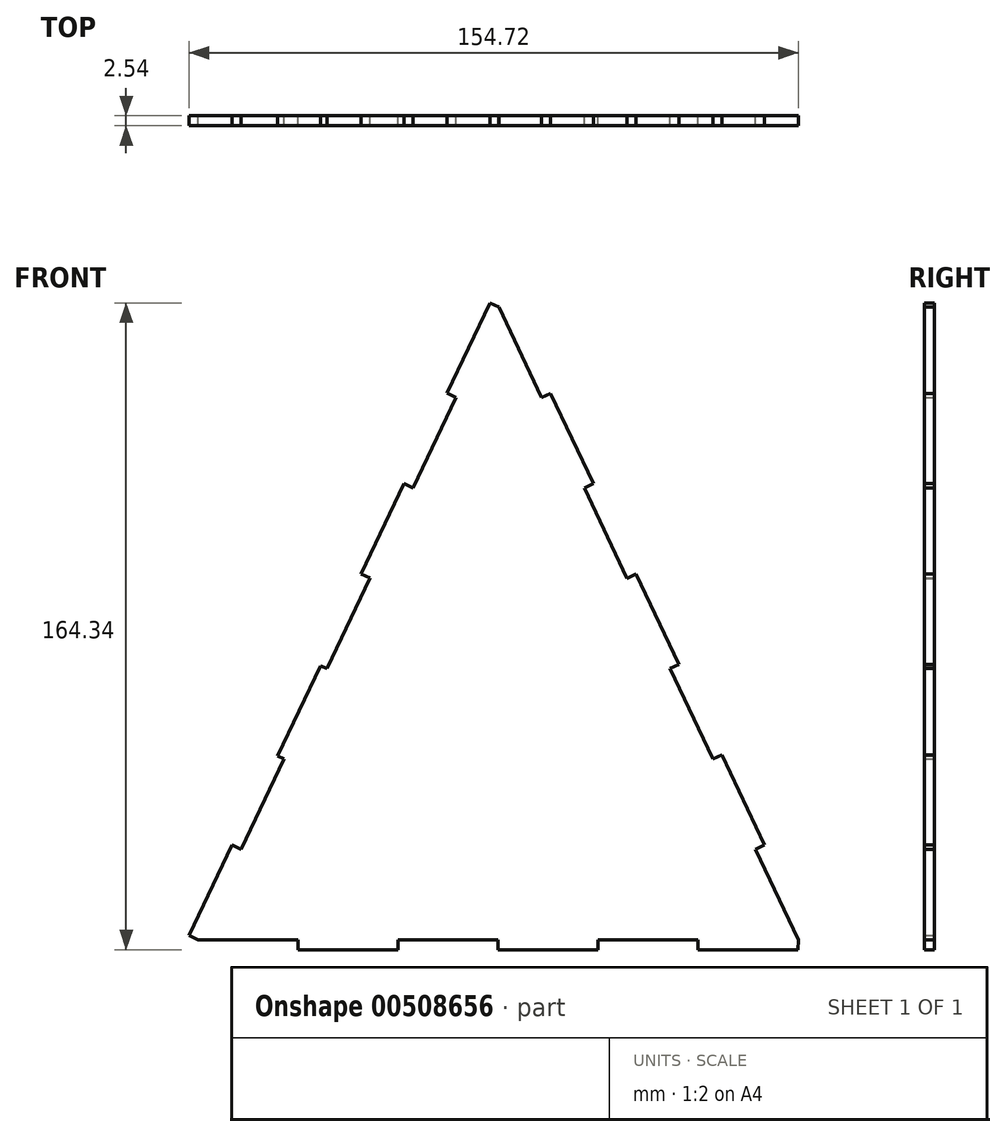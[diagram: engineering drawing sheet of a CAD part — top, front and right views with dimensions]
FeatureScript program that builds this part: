
annotation { "Feature Type Name" : "Feature", "Feature Type Description" : "" }
export const myFeature = defineFeature(function(context is Context, id is Id, definition is map)
    precondition{}
    {
        {
            var Q0;
            Q0=qCreatedBy(makeId("Front.planeOp"),FACE);
            var sketch = newSketch(context, id + "F0", { "sketchPlane" : qUnion([Q0])});
            skLineSegment(sketch, "E0", {"start": v(-10.9, 63.99) * mm, "end": v(-54.56, -27.9) * mm});
            skLineSegment(sketch, "E1", {"start": v(-76.36, -73.78) * mm, "end": v(76.06, -73.78) * mm});
            skLineSegment(sketch, "E2", {"start": v(76.06, -73.78) * mm, "end": v(0, 86.93) * mm});
            skLineSegment(sketch, "E3", {"start": v(0, 86.93) * mm, "end": v(-2.3, 88.02) * mm});
            skLineSegment(sketch, "E4", {"start": v(-2.3, 88.02) * mm, "end": v(-13.2, 65.08) * mm});
            skLineSegment(sketch, "E5", {"start": v(-13.2, 65.08) * mm, "end": v(-10.9, 63.99) * mm});
            skLineSegment(sketch, "E6", {"start": v(-24.1, 42.14) * mm, "end": v(-35, 19.2) * mm});
            skLineSegment(sketch, "E7", {"start": v(-35, 19.2) * mm, "end": v(-32.7, 18.1) * mm});
            skLineSegment(sketch, "E8", {"start": v(-43.6, -4.84) * mm, "end": v(-45.27, -4.19) * mm});
            skLineSegment(sketch, "E9", {"start": v(-45.27, -4.19) * mm, "end": v(-56.17, -27.13) * mm});
            skLineSegment(sketch, "E10", {"start": v(-56.17, -27.13) * mm, "end": v(-54.56, -27.9) * mm});
            skLineSegment(sketch, "E11", {"start": v(-54.56, -27.9) * mm, "end": v(-65.46, -50.84) * mm});
            skLineSegment(sketch, "E12", {"start": v(-65.46, -50.84) * mm, "end": v(-67.76, -49.75) * mm});
            skLineSegment(sketch, "E13", {"start": v(-67.76, -49.75) * mm, "end": v(-78.66, -72.7) * mm});
            skLineSegment(sketch, "E14", {"start": v(-78.66, -72.7) * mm, "end": v(-76.36, -73.78) * mm});
            skLineSegment(sketch, "E15", {"start": v(-76.36, -73.78) * mm, "end": v(-50.96, -73.78) * mm});
            skLineSegment(sketch, "E16", {"start": v(-50.96, -73.78) * mm, "end": v(-50.96, -76.32) * mm});
            skLineSegment(sketch, "E17", {"start": v(-50.96, -76.32) * mm, "end": v(-25.56, -76.32) * mm});
            skLineSegment(sketch, "E18", {"start": v(-25.56, -76.32) * mm, "end": v(-25.56, -73.78) * mm});
            skLineSegment(sketch, "E19", {"start": v(-25.56, -73.78) * mm, "end": v(-0.15, -73.78) * mm});
            skLineSegment(sketch, "E20", {"start": v(-0.15, -73.78) * mm, "end": v(-0.15, -76.32) * mm});
            skLineSegment(sketch, "E21", {"start": v(-0.15, -76.32) * mm, "end": v(25.25, -76.32) * mm});
            skLineSegment(sketch, "E22", {"start": v(25.25, -76.32) * mm, "end": v(25.25, -73.78) * mm});
            skLineSegment(sketch, "E23", {"start": v(25.25, -73.78) * mm, "end": v(50.65, -73.78) * mm});
            skLineSegment(sketch, "E24", {"start": v(50.65, -73.78) * mm, "end": v(50.65, -76.32) * mm});
            skPoint(sketch, "E25", {"position": v(78.35, 9.9) * mm});
            skLineSegment(sketch, "E26", {"start": v(50.65, -76.32) * mm, "end": v(76.05, -76.32) * mm});
            skLineSegment(sketch, "E27", {"start": v(76.05, -76.32) * mm, "end": v(76.06, -73.78) * mm});
            skLineSegment(sketch, "E28", {"start": v(76.06, -73.78) * mm, "end": v(65.2, -50.82) * mm});
            skLineSegment(sketch, "E29", {"start": v(65.2, -50.82) * mm, "end": v(67.5, -49.74) * mm});
            skLineSegment(sketch, "E30", {"start": v(67.5, -49.74) * mm, "end": v(56.62, -26.78) * mm});
            skLineSegment(sketch, "E31", {"start": v(56.62, -26.78) * mm, "end": v(54.33, -27.86) * mm});
            skLineSegment(sketch, "E32", {"start": v(43.46, -4.9) * mm, "end": v(45.76, -3.82) * mm});
            skLineSegment(sketch, "E33", {"start": v(45.76, -3.82) * mm, "end": v(34.9, 19.14) * mm});
            skLineSegment(sketch, "E34", {"start": v(34.9, 19.14) * mm, "end": v(32.6, 18.05) * mm});
            skLineSegment(sketch, "E35", {"start": v(21.73, 41.01) * mm, "end": v(24.03, 42.1) * mm});
            skLineSegment(sketch, "E36", {"start": v(24.03, 42.1) * mm, "end": v(13.16, 65.06) * mm});
            skLineSegment(sketch, "E37", {"start": v(13.16, 65.06) * mm, "end": v(10.87, 63.97) * mm});
            skLineSegment(sketch, "E38.trimOffspring", {"start": v(-65.46, -50.84) * mm, "end": v(-76.36, -73.78) * mm});
            skLineSegment(sketch, "E39", {"start": v(0, 86.93) * mm, "end": v(-10.9, 63.99) * mm});
            skLineSegment(sketch, "E40", {"start": v(-24.1, 42.14) * mm, "end": v(-21.8, 41.05) * mm});
            skSolve(sketch);
        }
        {
            var Q0;
            Q0 = qSketchRegion(id + "F0", true);
            extrude(context, id + "F1", {"entities" : qUnion([Q0]), "depth" : 2.54 * mm, "offsetDistance" : 25.4 * mm});
        }
    });
